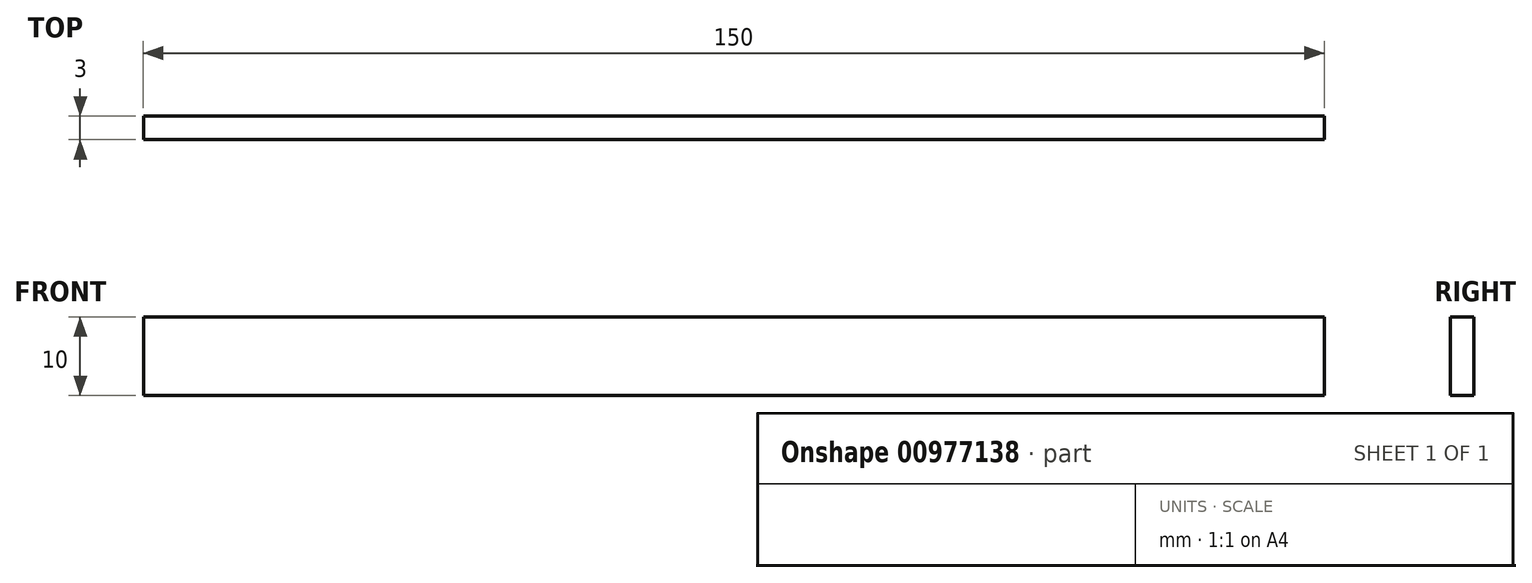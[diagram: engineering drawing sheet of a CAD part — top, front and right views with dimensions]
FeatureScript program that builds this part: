
annotation { "Feature Type Name" : "Feature", "Feature Type Description" : "" }
export const myFeature = defineFeature(function(context is Context, id is Id, definition is map)
    precondition{}
    {
        {
            var Q0;
            Q0=qCreatedBy(makeId("Front.planeOp"),FACE);
            var sketch = newSketch(context, id + "F0", { "sketchPlane" : qUnion([Q0])});
            skLineSegment(sketch, "E0", {"start": v(-75.63, 0) * mm, "end": v(74.37, 0) * mm});
            skLineSegment(sketch, "E1", {"start": v(-75.63, 0) * mm, "end": v(-75.63, -10) * mm});
            skLineSegment(sketch, "E2", {"start": v(74.37, 0) * mm, "end": v(74.37, -10) * mm});
            skLineSegment(sketch, "E3", {"start": v(-75.63, -10) * mm, "end": v(74.37, -10) * mm});
            skSolve(sketch);
        }
        {
            var Q0;
            Q0 = qSketchRegion(id + "F0", true);
            extrude(context, id + "F1", {"entities" : qUnion([Q0]), "depth" : 3 * mm, "offsetDistance" : 25 * mm});
        }
    });
